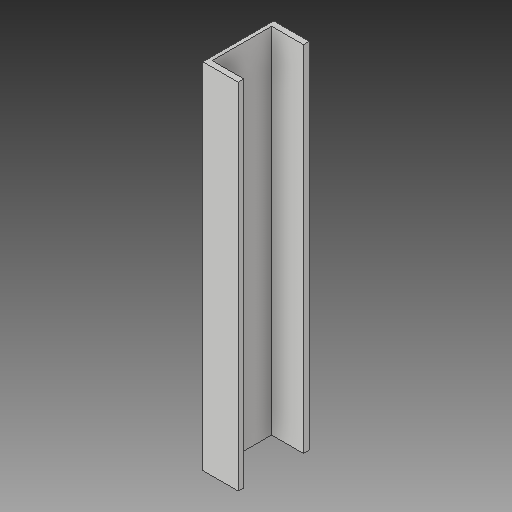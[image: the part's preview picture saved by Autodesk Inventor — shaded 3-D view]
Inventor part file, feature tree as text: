
AUTODESK INVENTOR PART (.ipt)
format: ipt  version: 2019 (Build 230136000, 136)  size: 91,136 bytes
history: native  units: in
note: dims shown in document units (in); Inventor stores cm internally (conversion verified against a paired STEP export)
features: other x3, sketch x1
ambient origin geometry x8: Origin, YZ Plane, XZ Plane, XY Plane, X Axis, Y Axis, Z Axis, Center Point
bodies: Solid1 (feature_tree)
feature tree (4):
  other  "Channel1_MIR.ipt"
  other  "Solid1::Channel1_MIR.ipt"
  other  "TaggingFeature1"
  sketch  "Sketch1"  dims[d0=0.3937in]
